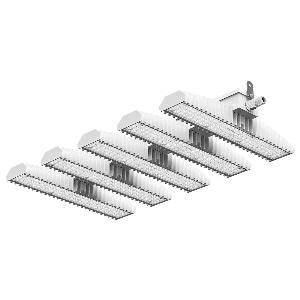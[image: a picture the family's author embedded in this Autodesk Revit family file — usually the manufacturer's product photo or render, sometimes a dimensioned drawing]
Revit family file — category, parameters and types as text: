
# Revit family: 3f_filippi_-_3f_lem_ampio_3f_filippi_-_58886_-_3f_lem_5_led_250_cr_ampio
name_source: partatom
category: Lighting Fixtures
units: mm (PartAtom-declared; Revit-internal decimal feet)

## family parameters
Cut with Voids When Loaded = No
Host = Face
Light Source = No
Part Type = Normal
Room Calculation Point = No
Round Connector Dimension = Use Diameter
Shared = No

## types (1)
- 3F Filippi - 3F LEM Ampio (1 x LED, 42473 lm, 274 W, 4000 K)
    Apparent Load = 274 VA
    Approval mark = CE
    CIE Flux Codes = 60 92 99 100 100
    Color Rendering = 80
    Color Temperature = 4000 K
    Control Gear = Electronic ballast
    Default Elevation = 1800 mm
    Description = Industrial luminaire with high light output and high luminous efficiency designed with the most innovative technologies for environments with temperature up to 55°C.

ILLUMINOTECHNICAL
Luminous efficiency 100% (DLOR 100%, ULOR 0%).
Initial luminous flux of the luminaire 42473 lm.
Direct symmetric wide distribution: the illuminated area has a rectangular shape.
Installation Interdistance Transv.D = 1.58 x hu - Long.D = 1.45 x hu.
Tabular UGR (CIE 117 - 4H-8H; S=0.25H; 70/50/20): RUG 23.2 - 24.2.
Beam angle: 93° - 99°.
Luminous efficacy 155 lm/W.
Lifetime (L93/B10): 30000 h. (tq+25°C)
Lifetime (L90/B10): 50000 h. (tq+25°C)
Lifetime (L85/B10): 80000 h. (tq+25°C)
Lifetime (L80/B10): 100000 h. (tq+25°C)
Lifetime (L85/B10): 50000 h. (tq+55°C)
Sudden decreased luminous flux after 50000 hours: 0% (C0).
Photobiological safety in compliance with IEC/TR 62778: RG0 risk exempt, (IEC 62471).
In compliance with IEC/EN 62722-2-1 - IEC/EN 62717 standards.

SOURCE
5 Mid-Power linear LED modules 50W/840.
Energy efficiency class (UE 2019/2020 - UE 2019/2015): C.
CIE 13.3 Colour rendering index: CRI >80 (R9 <50%).
IES TM-30 Fidelity Index: Rf = 84 Rg = 95.
CCT nominal colour temperature 4000 K.
Colour initial tolerance (MacAdam): SDCM 3.

MECHANICAL
Passive modular heatsinks in die-casted aluminium, painted in white colour.
To optimize the thermal management of the LED module, the heatsinks are oversized and provided with self-cleaning of cooling fins.
Wiring body in aluminium and galvanised steel anchored solidly to the sinks and thermally separated.
3F Lens lenses with high luminous efficiency, transparent methacrylate (PMMA), fixed to the LED modules.
Fixing brackets in stainless steel.
Luminaire with limited surface temperature. - D - (EN 60598-2-24)
Dimensions: 952x542 mm, height 129 mm. Weight 20.9 kg.
IP65 protection degree.
Mechanical strength to impacts IK06 (1 joule).
Glow-wire test resistance 650°C.

ELECTRICAL
Halogen Free electronic wiring 230V-50/60Hz, power factor 0.97, THD <25%, constant output current, class I, 3 driver.
Power of the luminaire 274 W.
ENEC - CE.
SAFE FLICKER: PstLM=<1 and SVM=<0.4 (IEC TR 61547-1 and IEC TR 63158), to ensure a more comfortable and safe light.
Luminaire compliant with EN 60598-2-22 for power supply from a centralised emergency system CPSS (Central Power Supply System), not incorporated in the luminaire - high risk areas excluded. The default power and flux are 100% in AC and 100% in DC.
Ambient temperature from -30°C to +55°C.
Temperature class T6 max 85°C.
Quick connection via M20 3P connector with 9-13 mm tightening range.
Power unit positioned on a separate compartment by the LED module to ensure optimum temperatures of cabling components, to be inspectable and maintainable.
Relative humidity UR: <85%.

INSTALLATION
Ceiling / Suspended / Wall.
All accessories dedicated to this product are available on the Catalog and on our website www.3F-Filippi.com.

APPLICATIONS
In commercial environments, exhibition and industrial areas, stores, open areas.
Applications with high ambient temperature up to 55°C.
Environments in which it is necessary a total protection against falling fragments (eg environments with foodstuffs or machines with moving parts or with extreme temperature changes), use luminaires with polycarbonate lenses.

WARNING
Fixture not suitable for cold stores with an ambient temperature <0°C and/or relative humidity >85%.
Luminaire designed for disposal/recycling at end-of-life.
Replaceable (LED only) light source by a professional. Replaceable control gear by a professional.
    Height = 129 mm
    Lamp = 1 x LED
    Lamp Light Flux = 42473 lm
    Lamp Power = 274 W
    Lamp count = 1
    Length = 952 mm
    Lifetime = 50000 h
    Luminous efficacy = 155 lm/W
    Manufacturer = 3F Filippi
    ModVariant = No
    Model = 3F Filippi - 58886 - 3F LEM 5 LED 250 CR AMPIO
    Mounting Place = Ceiling
    Mounting Type = Pendant
    Number of Poles = 1
    OnlyDefault = Yes
    Power Factor = 1
    Product Name = 3F Filippi - 3F LEM Ampio
    Product group = pendant luminaire
    ProductGroupID = 9
    Protection Class = Protection class I
    Protection Degree = IP 65
    RLX_Detail_Level = 1
    RLX_Emergency_Light_Flux = 0 lm
    RLX_Emergency_Type = 0
    RLX_Emergency_Type_DB = No
    RlxData = <blob elided: 132473 chars, md5=deb790d4>
    Socket = socket
    Standby Power = 0 W
    System Light Flux = 42473 lm
    System Power = 274 W
    Type Comments = Product without accessories
    Type Image = 3f_filippi_-_lem_5.jpg
    URL = http://relux.com
    VarID = ---
    Voltage = 0 V
    Weight = 0.00 kg
    Width = 542 mm

## geometry (parser evidence)
native form markers: Blend x4, Sweep x14
no freeform markers — native parametric forms only
